# Revit family: ALMA-Mira_Wall_Mixer_with_Turn_Divertor
name_source: partatom
category: Plumbing Equipment
units: mm (PartAtom-declared; Revit-internal decimal feet)

## family parameters
Classification = None
Cut with Voids When Loaded = Yes
Host = Face
Maintain Annotation Orientation = No
Part Type = Normal
Room Calculation Point = No
Round Connector Dimension = Use Diameter
Shared = No

## types (3) — shared parameters
Default Elevation = 1219 mm
Divertor Plate Width = 40 mm  [stored 0.131234 ft]
Divertor Width = 25 mm  [stored 0.082021 ft]
InWall_Material = BM_BRASS
Mixer Plate Width = 65 mm
Mixer Width = 45 mm  [stored 0.147638 ft]

## per-type parameters (varying)
| type | Mixer_Material |
| BRUSHED VINTAGE ANTIQUE BRASS (BWTDIVVB) | BM_ANTIQUE BRASS |
| BRUSHED BRASS GOLD (BWTDIVGD) | BM_BRASS GOLD |
| BRUSHED NICKEL (BWTDIVBN) | BM_NICKEL |

note: [stored X ft] marks values corroborated as IEEE doubles in the binary element streams (Revit-internal decimal feet)

## geometry (parser evidence)
native form markers: Sweep x1
no freeform markers — native parametric forms only
